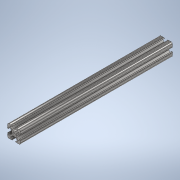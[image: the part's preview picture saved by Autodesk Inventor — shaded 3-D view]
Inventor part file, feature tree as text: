
AUTODESK INVENTOR PART (.ipt)
format: ipt  version: 2020 (Build 240168000, 168)  size: 239,104 bytes
history: native  units: in
note: dims shown in document units (in); Inventor stores cm internally (conversion verified against a paired STEP export)
features: extrude x1, sketch x1
ambient origin geometry x8: Origin, YZ Plane, XZ Plane, XY Plane, X Axis, Y Axis, Z Axis, Center Point
bodies: Solid1 (feature_tree)
feature tree (2):
  extrude  "Extrusion1"  [1 undecoded]
  sketch  "Sketch1"  dims[d0=12.0in d1=0.0in]
note: 1 required parameter value undecoded (feature->parameter linkage not recoverable at this tier; creation-order binding heuristic only, values carry confidence <= 0.55)
